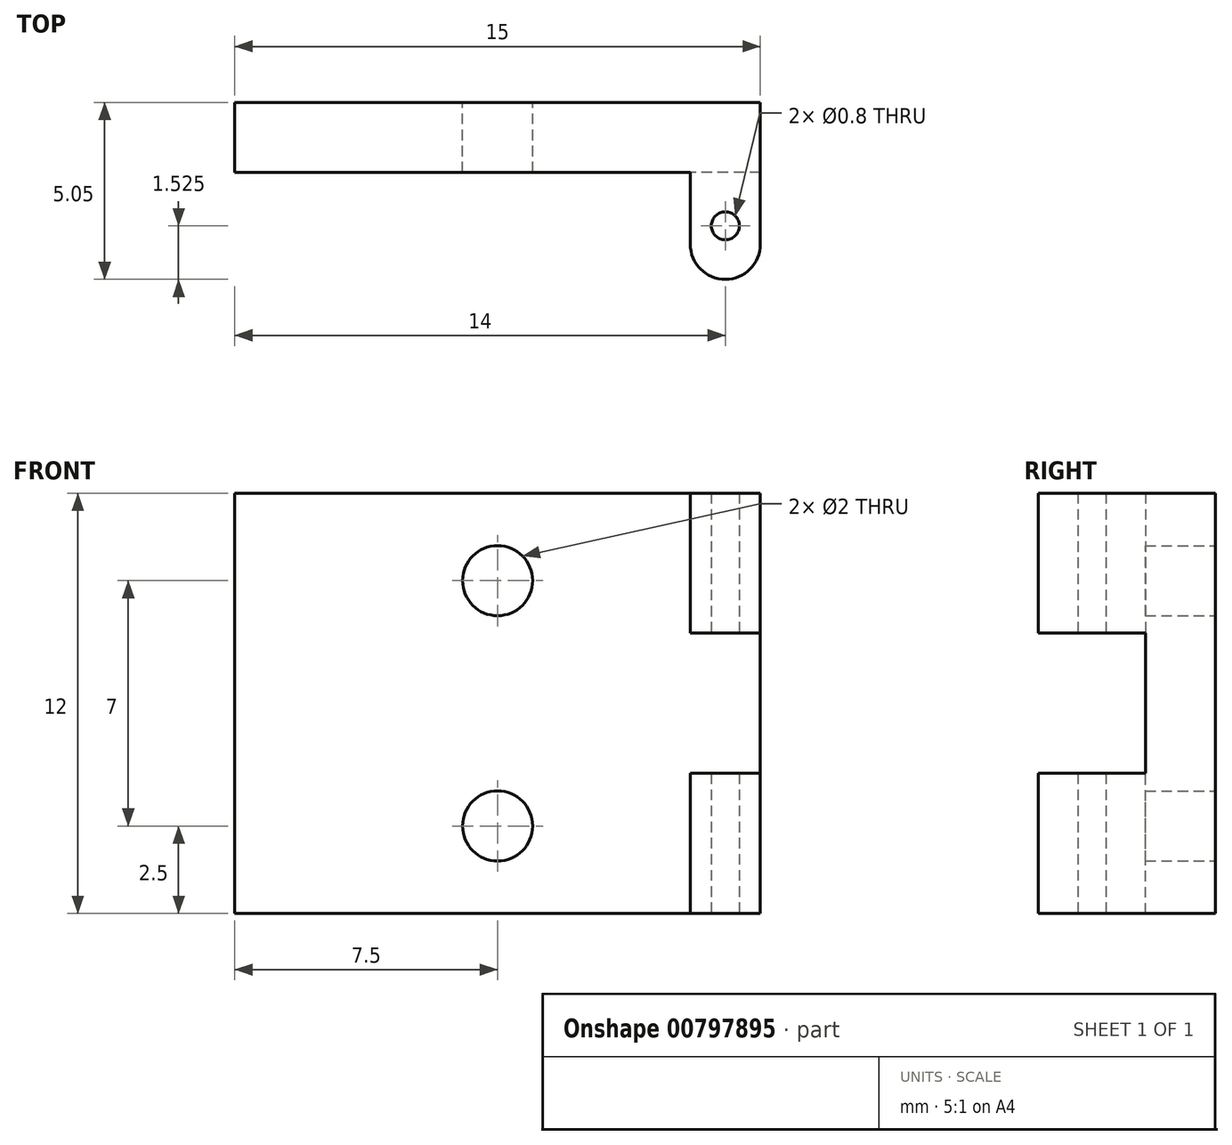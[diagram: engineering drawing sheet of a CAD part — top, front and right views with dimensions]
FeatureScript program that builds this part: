
annotation { "Feature Type Name" : "Feature", "Feature Type Description" : "" }
export const myFeature = defineFeature(function(context is Context, id is Id, definition is map)
    precondition{}
    {
        {
            var Q0;
            Q0=qCreatedBy(makeId("Front.planeOp"),FACE);
            var sketch = newSketch(context, id + "F0", { "sketchPlane" : qUnion([Q0])});
            skLineSegment(sketch, "E0.bottom", {"start": v(7.5, 6) * mm, "end": v(-7.5, 6) * mm});
            skLineSegment(sketch, "E0.top", {"start": v(7.5, -6) * mm, "end": v(-7.5, -6) * mm});
            skLineSegment(sketch, "E0.left", {"start": v(7.5, 6) * mm, "end": v(7.5, -6) * mm});
            skLineSegment(sketch, "E0.right", {"start": v(-7.5, 6) * mm, "end": v(-7.5, -6) * mm});
            skPoint(sketch, "E0.middle", {"position": v(0, 0) * mm});
            skSolve(sketch);
        }
        {
            var Q0;
            Q0 = qSketchRegion(id + "F0", true);
            extrude(context, id + "F1", {"entities" : qUnion([Q0]), "depth" : 2 * mm, "offsetDistance" : 25 * mm});
        }
        {
            var Q0;
            Q0=makeQuery(id+"F1.opExtrude","CAP_FACE",FACE,{"disambiguationData":[OSD([sQuery(id+"F0.wireOp",EDGE,"E0.bottom"),sQuery(id+"F0.wireOp",EDGE,"E0.top"),sQuery(id+"F0.wireOp",EDGE,"E0.left"),sQuery(id+"F0.wireOp",EDGE,"E0.right")])],"isStart":false});
            var sketch = newSketch(context, id + "F2", { "sketchPlane" : qUnion([Q0])});
            skLineSegment(sketch, "E1.bottom", {"start": v(7.5, 6) * mm, "end": v(5.5, 6) * mm});
            skLineSegment(sketch, "E1.top", {"start": v(7.5, 2) * mm, "end": v(5.5, 2) * mm});
            skLineSegment(sketch, "E1.left", {"start": v(7.5, 6) * mm, "end": v(7.5, 2) * mm});
            skLineSegment(sketch, "E1.right", {"start": v(5.5, 6) * mm, "end": v(5.5, 2) * mm});
            skLineSegment(sketch, "E2.bottom", {"start": v(7.5, -6) * mm, "end": v(5.5, -6) * mm});
            skLineSegment(sketch, "E2.top", {"start": v(7.5, -2) * mm, "end": v(5.5, -2) * mm});
            skLineSegment(sketch, "E2.left", {"start": v(7.5, -6) * mm, "end": v(7.5, -2) * mm});
            skLineSegment(sketch, "E2.right", {"start": v(5.5, -6) * mm, "end": v(5.5, -2) * mm});
            skSolve(sketch);
        }
        {
            var Q0;
            Q0 = qSketchRegion(id + "F2", true);
            extrude(context, id + "F3", {"entities" : qUnion([Q0]), "operationType" : NewBodyOperationType.ADD, "depth" : 3.05 * mm, "offsetDistance" : 25 * mm});
        }
        {
            var Q0;
            Q0=makeQuery(id+"F3.boolean.opBoolean","MERGE",FACE,{"derivedFrom":[makeQuery(id+"F1.opExtrude","SWEPT_FACE",FACE,{"disambiguationData":[OSD([sQuery(id+"F0.wireOp",EDGE,"E0.top")])]}),makeQuery(id+"F3.opExtrude","SWEPT_FACE",FACE,{"disambiguationData":[OSD([sQuery(id+"F2.wireOp",EDGE,"E2.bottom")])]})]});
            var sketch = newSketch(context, id + "F4", { "sketchPlane" : qUnion([Q0])});
            skLineSegment(sketch, "E3.bottom", {"start": v(5.5, 5.05) * mm, "end": v(7.5, 5.05) * mm, "construction": true});
            skLineSegment(sketch, "E3.top", {"start": v(5.5, 2) * mm, "end": v(7.5, 2) * mm, "construction": true});
            skLineSegment(sketch, "E3.left", {"start": v(5.5, 5.05) * mm, "end": v(5.5, 2) * mm, "construction": true});
            skLineSegment(sketch, "E3.right", {"start": v(7.5, 5.05) * mm, "end": v(7.5, 2) * mm, "construction": true});
            skLineSegment(sketch, "E4", {"start": v(5.5, 5.05) * mm, "end": v(7.5, 2) * mm, "construction": true});
            skCircle(sketch, "E5", {"center": v(6.5, 3.52) * mm, "radius": 0.4 * mm});
            skSolve(sketch);
        }
        {
            var Q0;
            Q0 = qSketchRegion(id + "F4", true);
            extrude(context, id + "F5", {"entities" : qUnion([Q0]), "operationType" : NewBodyOperationType.REMOVE, "oppositeDirection" : true, "depth" : 25 * mm, "offsetDistance" : 25 * mm});
        }
        {
            var Q0;
            Q0=makeQuery(id+"F3.opExtrude","CAP_EDGE",EDGE,{"disambiguationData":[OSD([sQuery(id+"F2.wireOp",EDGE,"E1.left")])],"isStart":false});
            var Q1;
            Q1=makeQuery(id+"F3.opExtrude","CAP_EDGE",EDGE,{"disambiguationData":[OSD([sQuery(id+"F2.wireOp",EDGE,"E1.right")])],"isStart":false});
            var Q2;
            Q2=makeQuery(id+"F3.opExtrude","CAP_EDGE",EDGE,{"disambiguationData":[OSD([sQuery(id+"F2.wireOp",EDGE,"E2.left")])],"isStart":false});
            var Q3;
            Q3=makeQuery(id+"F3.opExtrude","CAP_EDGE",EDGE,{"disambiguationData":[OSD([sQuery(id+"F2.wireOp",EDGE,"E2.right")])],"isStart":false});
            fillet(context, id + "F6", {"entities" : qUnion([Q0, Q1, Q2, Q3]), "radius" : 1 * mm, "tangentPropagation" : true, "allowEdgeOverflow" : false});
        }
        {
            var Q0;
            Q0=makeQuery(id+"F1.opExtrude","CAP_FACE",FACE,{"disambiguationData":[OSD([sQuery(id+"F0.wireOp",EDGE,"E0.bottom"),sQuery(id+"F0.wireOp",EDGE,"E0.top"),sQuery(id+"F0.wireOp",EDGE,"E0.left"),sQuery(id+"F0.wireOp",EDGE,"E0.right")])],"isStart":true});
            var sketch = newSketch(context, id + "F7", { "sketchPlane" : qUnion([Q0])});
            skLineSegment(sketch, "E6", {"start": v(0, -3.5) * mm, "end": v(0, 3.5) * mm, "construction": true});
            skCircle(sketch, "E7", {"center": v(0, 3.5) * mm, "radius": 1 * mm});
            skCircle(sketch, "E8", {"center": v(0, -3.5) * mm, "radius": 1 * mm});
            skSolve(sketch);
        }
        {
            var Q0;
            Q0 = qSketchRegion(id + "F7", true);
            extrude(context, id + "F8", {"entities" : qUnion([Q0]), "operationType" : NewBodyOperationType.REMOVE, "oppositeDirection" : true, "depth" : 25 * mm, "offsetDistance" : 25 * mm});
        }
    });
